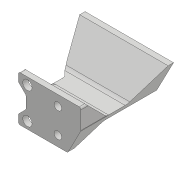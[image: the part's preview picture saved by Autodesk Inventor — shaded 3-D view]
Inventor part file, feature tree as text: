
AUTODESK INVENTOR PART (.ipt)
format: ipt  version: 2018 (Build 220112000, 112)  size: 603,136 bytes
history: native  units: mm
features: sketch x15, extrude x12, projected_geometry x10, hole x4, fillet x4, chamfer x3, plane x1, mirror x1
ambient origin geometry x8: Origin, YZ Plane, XZ Plane, XY Plane, X Axis, Y Axis, Z Axis, Center Point
bodies: Solid1 (feature_tree)
feature tree (50):
  extrude  "Extrusion1"  Depth=143.6mm
  hole  "Hole1"  [1 undecoded]
  extrude  "Extrusion2"  Depth=40.0mm
  extrude  "Extrusion5"  Depth=38.0mm
  extrude  "Extrusion3"  Depth=3.0mm TaperAngle=0.0deg
  extrude  "Extrusion4"  Depth=3.0mm TaperAngle=0.0deg
  sketch  "Sketch8"  dims[d18=41.0mm d20=3.0mm d21=0.0mm]
  hole  "Hole2"  [1 undecoded]
  hole  "Hole3"  [1 undecoded]
  extrude  "Extrusion6"  Depth=17.0624mm
  extrude  "Extrusion7"  Depth=46.0mm
  extrude  "Extrusion10"  Depth=3.0mm TaperAngle=0.0deg
  chamfer  "Chamfer3"  Distance=7.0mm
  plane  "Work Plane1"
  extrude  "Extrusion11"  Depth=10.0mm
  fillet  "Fillet1"  Radius=4.957359mm
  extrude  "Extrusion12"  Depth=10.0mm TaperAngle=0.0deg
  chamfer  "Chamfer4"  Distance=4.957359mm
  chamfer  "Chamfer5"  [1 undecoded]
  fillet  "Fillet2"  Radius=11.2mm
  fillet  "Fillet3"  Radius=10.0mm
  extrude  "Extrusion13"  [1 undecoded]
  fillet  "Fillet4"  Radius=8.0mm
  hole  "Hole4"  [1 undecoded]
  mirror  "Mirror2"
  extrude  "Extrusion14"  Depth=10.0mm
  sketch  "Sketch1"  dims[d0=76.0mm d1=143.6mm]
  sketch  "Sketch2"  dims[d2=3.0mm d3=0.0mm d4=8.0mm]
  sketch  "Sketch4"  dims[d5=70.0mm d6=40.0mm]
  sketch  "Sketch5"  dims[d7=3.2mm d8=6.0mm d9=6.3mm d10=2.0mm d11=90.0deg d12=8.0mm d13=20.594885mm d14=38.0mm]
  projected_geometry  "Projected Loop1"
  sketch  "Sketch7"  dims[d15=17.0mm d16=3.0mm d17=0.0mm]
  projected_geometry  "Projected Loop3"
  projected_geometry  "Projected Loop4"
  sketch  "Sketch10"  dims[d22=25.4mm d23=3.0mm d24=0.0mm]
  projected_geometry  "Projected Loop5"
  sketch  "Sketch11"  dims[d25=14.0mm d26=12.7mm]
  projected_geometry  "Projected Loop6"
  sketch  "Sketch12"  dims[d27=17.4625mm d30=17.0624mm]
  projected_geometry  "Projected Loop7"
  sketch  "Sketch16"  dims[d31=5.0mm]
  projected_geometry  "Projected Loop11"
  projected_geometry  "Projected Loop12"
  sketch  "Sketch17"  dims[d32=4.3mm d33=6.0mm d34=9.4mm d35=2.0mm d36=90.0deg d37=8.0mm d38=20.594885mm]
  projected_geometry  "Projected Loop13"
  sketch  "Sketch18"  dims[d39=5.3mm d40=6.0mm d41=10.4mm d42=2.0mm d43=90.0deg d44=8.0mm d45=20.594885mm d46=46.0mm]
  projected_geometry  "Projected Loop14"
  sketch  "Sketch19"  dims[d47=24.0mm d48=3.0mm d49=0.0mm]
  sketch  "Sketch20"  dims[d50=135.0deg]
  sketch  "Sketch21"  dims[d51=135.0deg d52=7.0mm d53=6.0mm d54=4.957359mm d55=50.0mm d56=0.0mm d57=4.957359mm d58=0.0mm d59=0.0mm d71=11.2mm d72=0.0mm d73=11.2mm d74=10.0mm d75=45.0deg d76=-18.0mm d77=8.0mm d78=8.0mm d79=9.5mm d80=9.5mm d81=15.0mm d82=0.0mm d83=2.0mm d84=18.0mm d85=15.0mm d86=0.0mm d87=15.0mm d88=10.0mm d89=45.0deg d90=4.24mm d91=10.0mm d92=45.0deg d93=1.0mm d94=3.0mm d95=15.0mm d96=0.0mm d97=1.0mm d98=26.0mm d99=10.0mm d100=12.0mm d101=2.459mm d102=6.0mm d103=10.4mm d104=2.0mm d105=90.0deg d106=10.0mm d107=20.594885mm d108=10.0mm d109=0.0mm]
note: 6 required parameter values undecoded (feature->parameter linkage not recoverable at this tier; creation-order binding heuristic only, values carry confidence <= 0.55)
